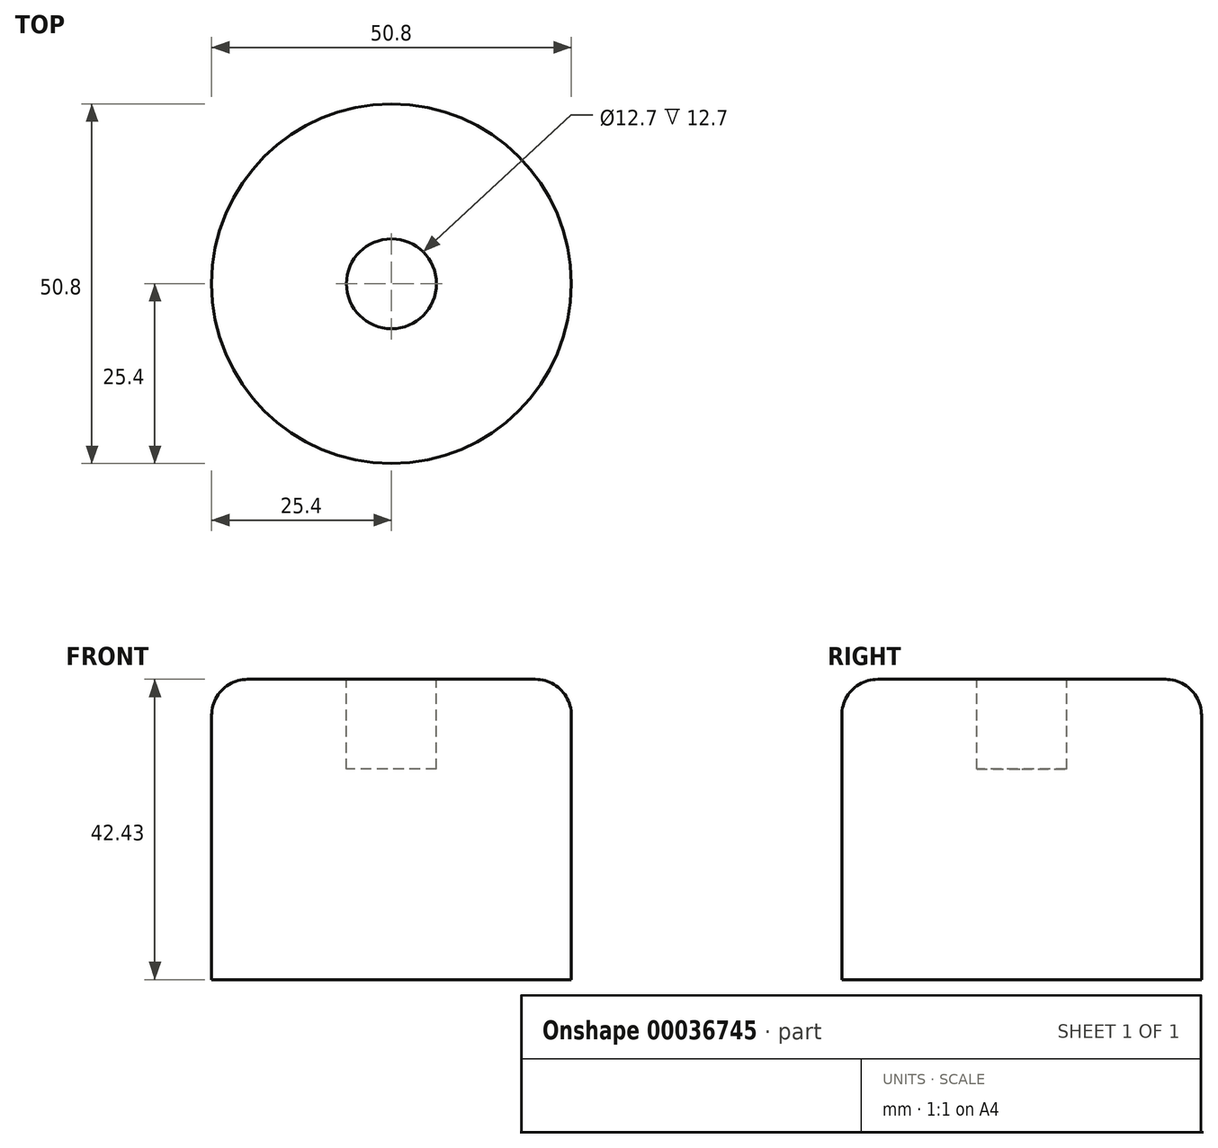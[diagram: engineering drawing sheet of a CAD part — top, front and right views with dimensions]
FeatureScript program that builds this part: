
annotation { "Feature Type Name" : "Feature", "Feature Type Description" : "" }
export const myFeature = defineFeature(function(context is Context, id is Id, definition is map)
    precondition{}
    {
        {
            var Q0;
            Q0=qCreatedBy(makeId("Top.planeOp"),FACE);
            var sketch = newSketch(context, id + "F0", { "sketchPlane" : qUnion([Q0])});
            skCircle(sketch, "E0", {"center": v(0, 0) * mm, "radius": 25.4 * mm});
            skSolve(sketch);
        }
        {
            var Q0;
            Q0 = qSketchRegion(id + "F0", true);
            extrude(context, id + "F1", {"entities" : qUnion([Q0]), "depth" : 42.43 * mm});
        }
        {
            var Q0;
            Q0=makeQuery(id+"F1.opExtrude","CAP_FACE",FACE,{"disambiguationData":[OSD([sQuery(id+"F0.wireOp",EDGE,"E0")])],"isStart":false});
            var sketch = newSketch(context, id + "F2", { "sketchPlane" : qUnion([Q0])});
            skCircle(sketch, "E1", {"center": v(0, 0) * mm, "radius": 6.35 * mm});
            skSolve(sketch);
        }
        {
            var Q0;
            Q0 = qSketchRegion(id + "F2", true);
            extrude(context, id + "F3", {"entities" : qUnion([Q0]), "operationType" : NewBodyOperationType.REMOVE, "oppositeDirection" : true, "depth" : 12.7 * mm});
        }
        {
            var Q0;
            Q0=makeQuery(id+"F1.opExtrude","CAP_EDGE",EDGE,{"disambiguationData":[OSD([sQuery(id+"F0.wireOp",EDGE,"E0")])],"isStart":false});
            fillet(context, id + "F4", {"entities" : qUnion([Q0]), "radius" : 5.08 * mm, "tangentPropagation" : true, "allowEdgeOverflow" : false});
        }
    });
